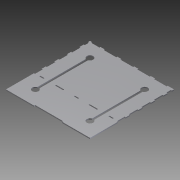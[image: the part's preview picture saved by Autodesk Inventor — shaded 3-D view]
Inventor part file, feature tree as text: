
AUTODESK INVENTOR PART (.ipt)
format: ipt  version: 2011 (Build 150239000, 239)  size: 1,059,840 bytes
history: native  units: in
note: dims shown in document units (in); Inventor stores cm internally (conversion verified against a paired STEP export)
features: sketch x31, extrude x30, fillet x2
ambient origin geometry x8: Origin, YZ Plane, XZ Plane, XY Plane, X Axis, Y Axis, Z Axis, Center Point
bodies: Solid1 (feature_tree)
feature tree (63):
  sketch  "Sketch1"  dims[d0=20.0in d1=20.0in]
  extrude  "Extrusion1"  Depth=20.0in
  extrude  "Extrusion2"  Depth=3.5in
  extrude  "Extrusion3"  Depth=3.5in
  extrude  "Extrusion4"  Depth=3.5in
  extrude  "Extrusion5"  Depth=3.5in
  extrude  "Extrusion6"  Depth=1.911in
  extrude  "Extrusion7"  Depth=5.089in
  extrude  "Extrusion8"  Depth=5.089in
  extrude  "Extrusion9"  Depth=1.911in
  extrude  "Extrusion10"  Depth=0.156in
  extrude  "Extrusion11"  Depth=0.156in
  extrude  "Extrusion12"  Depth=0.156in
  extrude  "Extrusion13"  Depth=0.156in
  extrude  "Extrusion14"  Depth=0.156in
  extrude  "Extrusion15"  Depth=0.156in
  fillet  "Fillet1"  Radius=0.156in
  fillet  "Fillet2"  Radius=0.156in
  extrude  "Extrusion16"  Depth=0.156in
  extrude  "Extrusion17"  Depth=1.0in
  extrude  "Extrusion18"  Depth=1.0in
  extrude  "Extrusion19"  Depth=0.5in TaperAngle=0.0deg
  extrude  "Extrusion20"  Depth=0.5in
  extrude  "Extrusion21"  Depth=1.5in
  extrude  "Extrusion22"  Depth=1.5in
  extrude  "Extrusion23"  Depth=1.5in
  extrude  "Extrusion24"  Depth=1.5in
  extrude  "Extrusion25"  Depth=1.5in
  extrude  "Extrusion26"  Depth=1.5in
  extrude  "Extrusion27"  Depth=1.5in
  extrude  "Extrusion28"  Depth=1.0in TaperAngle=0.0deg
  extrude  "Extrusion29"  Depth=0.5in TaperAngle=0.0deg
  extrude  "Extrusion30"  Depth=0.25in TaperAngle=0.0deg
  sketch  "Sketch2"  dims[d2=3.5in d3=3.5in]
  sketch  "Sketch3"  dims[d4=3.5in d5=3.5in]
  sketch  "Sketch4"  dims[d6=3.5in d7=3.5in]
  sketch  "Sketch5"  dims[d8=3.5in d9=3.5in]
  sketch  "Sketch6"  dims[d10=1.911in d11=1.911in]
  sketch  "Sketch7"  dims[d12=1.911in d13=5.089in]
  sketch  "Sketch8"  dims[d14=5.089in d15=5.089in]
  sketch  "Sketch9"  dims[d16=5.089in d17=1.911in]
  sketch  "Sketch10"  dims[d18=1.911in d19=0.156in]
  sketch  "Sketch11"  dims[d20=0.156in d21=0.156in]
  sketch  "Sketch12"  dims[d22=0.156in d23=0.156in]
  sketch  "Sketch13"  dims[d24=0.156in d25=0.156in]
  sketch  "Sketch14"  dims[d26=0.156in d27=0.156in]
  sketch  "Sketch15"  dims[d28=0.156in d29=0.156in d30=0.156in d31=0.156in]
  sketch  "Sketch16"  dims[d32=0.156in d33=0.156in]
  sketch  "Sketch17"  dims[d34=0.156in d35=1.0in]
  sketch  "Sketch18"  dims[d36=1.0in d37=1.0in]
  sketch  "Sketch19"  dims[d38=1.0in d39=0.5in d40=0.0in]
  sketch  "Sketch20"  dims[d41=0.5in d42=0.5in]
  sketch  "Sketch21"  dims[d43=1.0in d44=1.5in]
  sketch  "Sketch22"  dims[d45=1.0in d46=1.5in]
  sketch  "Sketch23"  dims[d47=1.0in d48=1.5in]
  sketch  "Sketch24"  dims[d49=1.0in d50=1.5in]
  sketch  "Sketch25"  dims[d51=1.0in d52=1.5in]
  sketch  "Sketch26"  dims[d53=1.0in d54=1.5in]
  sketch  "Sketch27"  dims[d55=1.0in d56=1.5in]
  sketch  "Sketch28"  dims[d57=1.0in d58=1.0in d59=0.0in]
  sketch  "Sketch29"  dims[d60=1.0in d61=0.0in d62=0.5in d63=0.0in]
  sketch  "Sketch30"  dims[d64=0.5in d65=0.0in d66=0.25in d67=0.0in]
  sketch  "Sketch31"  dims[d68=10.0in d69=2.6in d70=5.2in d71=7.4in d72=5.2in d73=0.25in d74=0.25in d75=0.25in d76=0.25in d77=0.25in d78=0.25in d79=0.25in d80=0.25in d81=0.25in d82=0.25in d83=0.25in d84=0.25in d85=0.25in d86=0.0in d87=1.5in d88=1.5in d89=1.5in d90=1.5in d91=0.25in d92=0.25in d93=0.25in d94=0.25in d95=0.25in d96=0.25in d97=0.25in d98=0.25in d99=0.25in d100=0.25in d101=0.25in d102=0.25in d103=0.0in d104=0.25in d105=0.0in d106=1.0in d107=1.0in d108=1.0in d109=1.0in d110=1.0in d111=1.0in d112=1.0in d113=1.0in d114=1.0in d115=1.0in d116=1.0in d117=1.0in d118=1.0in d119=1.0in d120=1.0in d121=1.0in d122=1.0in d123=1.0in d124=1.0in d125=1.0in d126=0.25in d127=1.0in d128=0.0in d129=1.0in d130=0.0in d131=1.0in d132=0.0in d133=0.5in d134=0.5in d135=0.5in d136=0.5in d137=1.0in d138=0.0in d139=1.5in d140=0.25in d141=0.0in d142=0.125in d143=0.25in d144=0.125in d145=0.25in d146=0.25in d147=0.0in d148=0.5in d149=0.5in d150=0.25in d151=0.5in d152=1.0in d153=0.0in d154=0.25in d155=0.5in d156=1.0in d157=0.0in d158=6.45in d159=0.25in d160=0.0in d161=1.25in d162=1.0in d163=2.0in d164=1.0in d165=2.0in d166=1.0in d167=2.0in d168=1.0in d169=0.25in d170=0.0in d171=0.5in d172=0.25in d173=0.0in d174=0.25in d175=0.25in d176=1.0in d177=3.0in d178=1.0in d179=3.0in d180=1.0in d181=3.0in d182=1.0in d183=3.0in d184=1.0in d185=0.25in d186=0.0in d187=0.5in d188=0.5in d189=0.25in d190=0.0in d191=0.25in d192=0.0in d193=0.25in d194=0.0in d195=1.0in d196=0.25in d197=1.0in d198=1.0in d199=1.0in d200=1.75in d201=1.0in d202=1.75in d203=1.0in d204=3.0in d205=1.0in d206=0.25in d207=0.0in d208=0.5in d209=2.0in d210=0.5in d211=2.0in d212=0.25in d213=0.0in d214=0.25in d215=0.0in d216=0.25in d217=0.0in d218=0.25in d219=0.0in d220=1.594in d221=1.594in d222=3.188in d223=3.188in d224=1.594in d225=1.594in d226=3.188in d227=3.188in d228=0.156in d229=0.156in d230=0.156in d231=0.156in d232=0.156in d233=0.156in d234=0.156in d235=0.156in d236=0.25in d237=0.0in]
